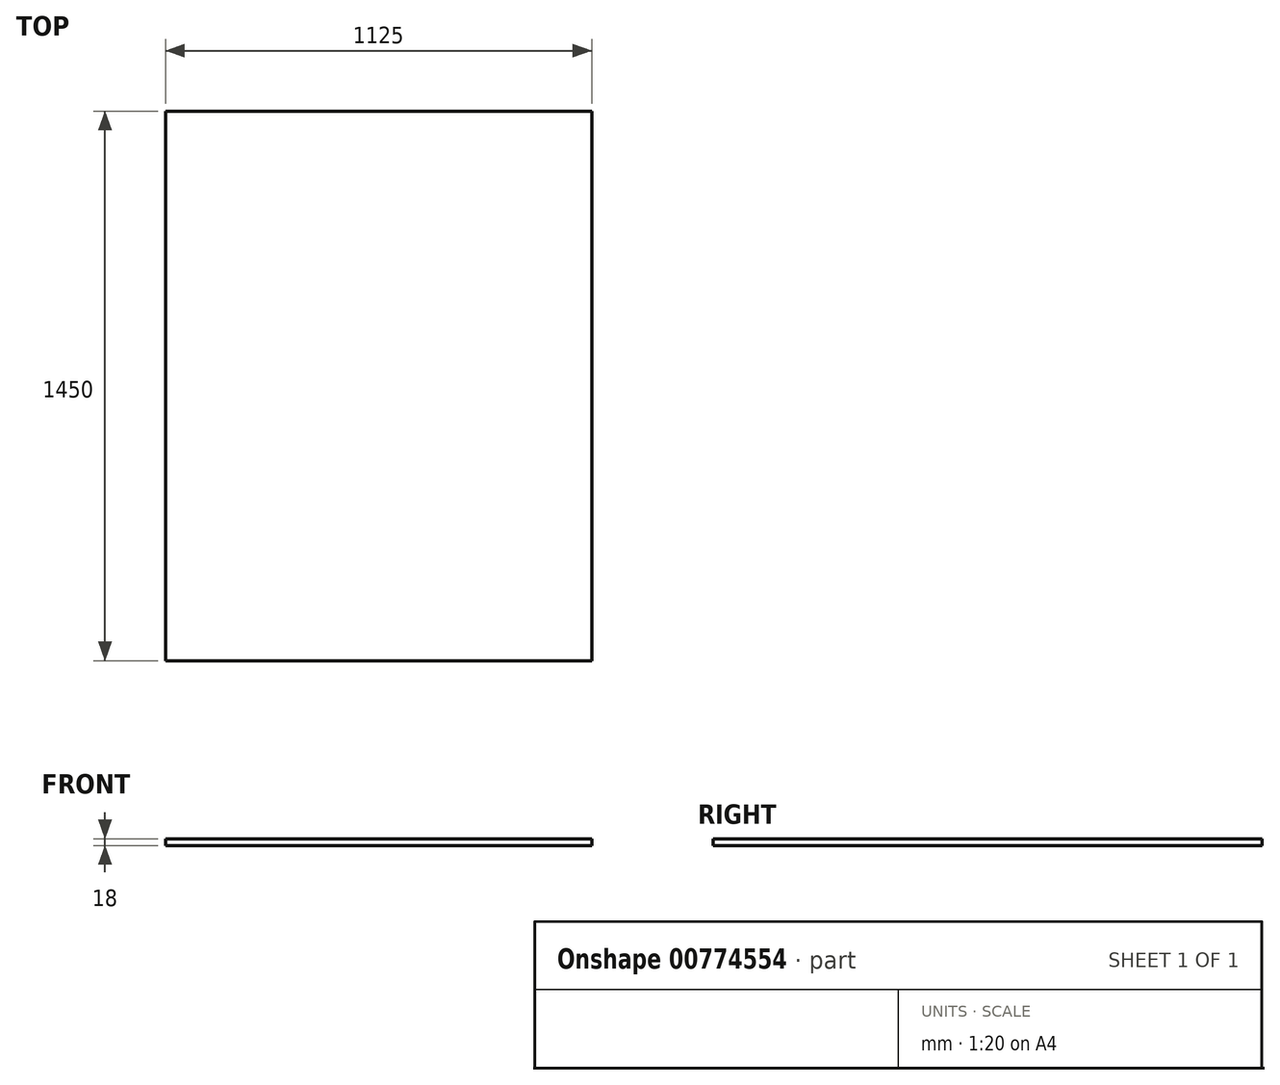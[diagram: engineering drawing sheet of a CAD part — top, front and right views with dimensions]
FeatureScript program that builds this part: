
annotation { "Feature Type Name" : "Feature", "Feature Type Description" : "" }
export const myFeature = defineFeature(function(context is Context, id is Id, definition is map)
    precondition{}
    {
        {
            var Q0;
            Q0=qCreatedBy(makeId("Front.planeOp"),FACE);
            var sketch = newSketch(context, id + "F0", { "sketchPlane" : qUnion([Q0])});
            skLineSegment(sketch, "E0.bottom", {"start": v(562.5, -9) * mm, "end": v(-562.5, -9) * mm});
            skLineSegment(sketch, "E0.top", {"start": v(562.5, 9) * mm, "end": v(-562.5, 9) * mm});
            skLineSegment(sketch, "E0.left", {"start": v(562.5, -9) * mm, "end": v(562.5, 9) * mm});
            skLineSegment(sketch, "E0.right", {"start": v(-562.5, -9) * mm, "end": v(-562.5, 9) * mm});
            skPoint(sketch, "E0.middle", {"position": v(0, 0) * mm});
            skSolve(sketch);
        }
        {
            var Q0;
            Q0 = qSketchRegion(id + "F0", true);
            extrude(context, id + "F1", {"entities" : qUnion([Q0]), "depth" : 1450 * mm, "offsetDistance" : 25 * mm});
        }
    });
